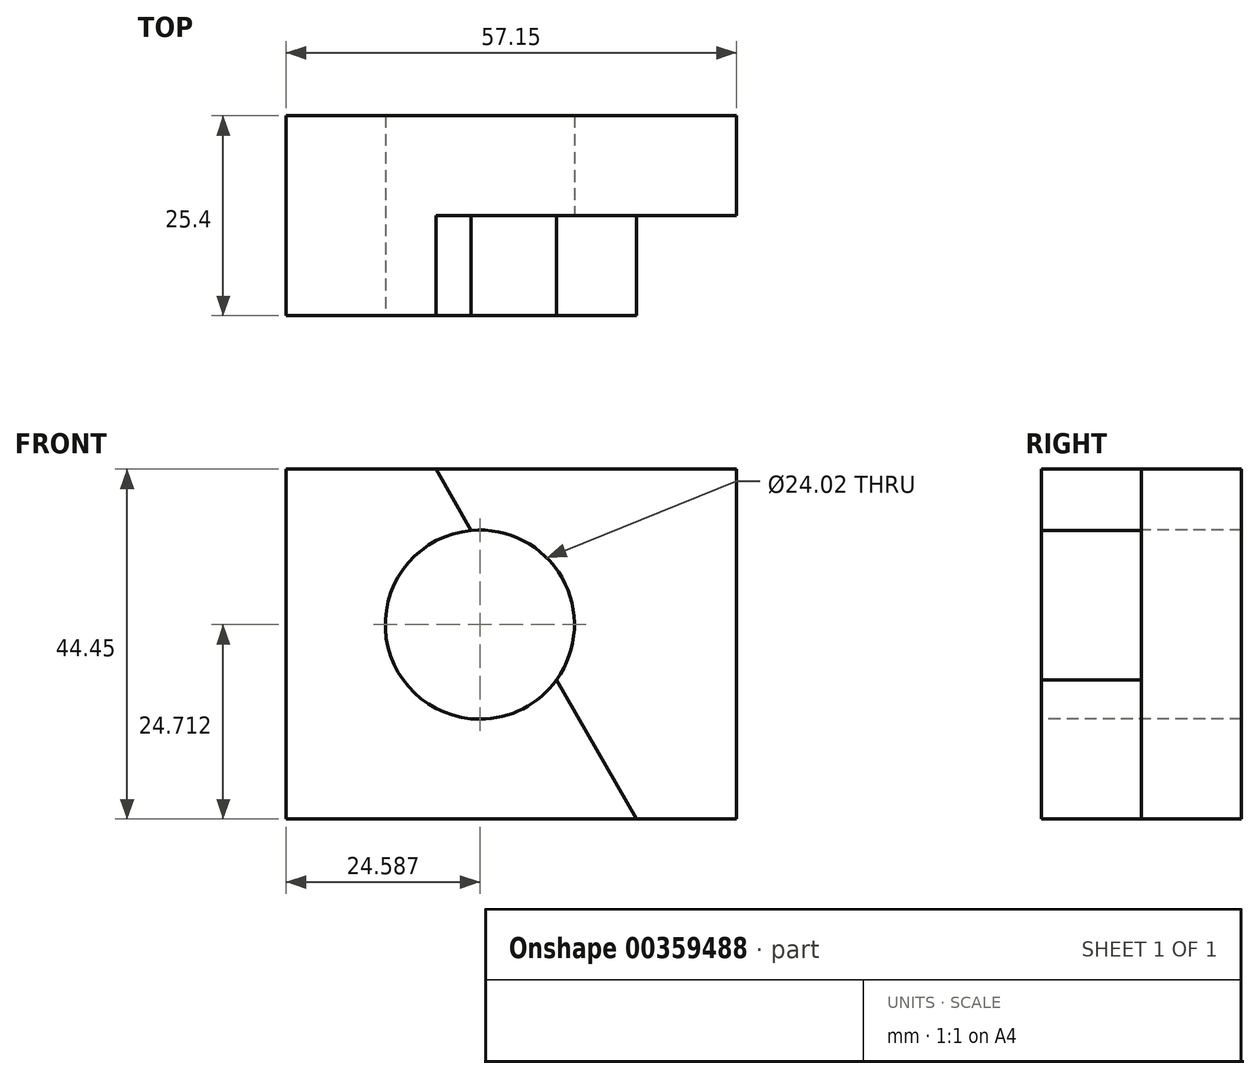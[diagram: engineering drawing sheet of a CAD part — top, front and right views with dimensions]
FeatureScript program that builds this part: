
annotation { "Feature Type Name" : "Feature", "Feature Type Description" : "" }
export const myFeature = defineFeature(function(context is Context, id is Id, definition is map)
    precondition{}
    {
        {
            var Q0;
            Q0=qCreatedBy(makeId("Front.planeOp"),FACE);
            var sketch = newSketch(context, id + "F0", { "sketchPlane" : qUnion([Q0])});
            skLineSegment(sketch, "E0", {"start": v(0, 44.45) * mm, "end": v(0, 0) * mm});
            skLineSegment(sketch, "E1", {"start": v(0, 0) * mm, "end": v(57.15, 0) * mm});
            skLineSegment(sketch, "E2", {"start": v(57.15, 0) * mm, "end": v(57.15, 44.45) * mm});
            skLineSegment(sketch, "E3", {"start": v(57.15, 44.45) * mm, "end": v(0, 44.45) * mm});
            skSolve(sketch);
        }
        {
            var Q0;
            Q0 = qSketchRegion(id + "F0", true);
            extrude(context, id + "F1", {"entities" : qUnion([Q0]), "oppositeDirection" : true, "depth" : 25.4 * mm});
        }
        {
            var Q0;
            Q0=qCreatedBy(makeId("Front.planeOp"),FACE);
            var sketch = newSketch(context, id + "F2", { "sketchPlane" : qUnion([Q0])});
            skLineSegment(sketch, "E4", {"start": v(44.45, 44.45) * mm, "end": v(44.45, 0) * mm});
            skLineSegment(sketch, "E5", {"start": v(44.45, 0) * mm, "end": v(57.15, 0) * mm});
            skLineSegment(sketch, "E6", {"start": v(57.15, 0) * mm, "end": v(57.15, 44.45) * mm});
            skLineSegment(sketch, "E7", {"start": v(57.15, 44.45) * mm, "end": v(44.45, 44.45) * mm});
            skSolve(sketch);
        }
        {
            var Q0;
            Q0 = qSketchRegion(id + "F2", true);
            extrude(context, id + "F3", {"entities" : qUnion([Q0]), "operationType" : NewBodyOperationType.REMOVE, "oppositeDirection" : true, "depth" : 12.7 * mm});
        }
        {
            var Q0;
            Q0=qCreatedBy(makeId("Front.planeOp"),FACE);
            var sketch = newSketch(context, id + "F4", { "sketchPlane" : qUnion([Q0])});
            skLineSegment(sketch, "E8", {"start": v(44.45, 0) * mm, "end": v(44.45, 44.45) * mm});
            skLineSegment(sketch, "E9", {"start": v(44.45, 44.45) * mm, "end": v(19.05, 44.45) * mm});
            skLineSegment(sketch, "E10", {"start": v(19.05, 44.45) * mm, "end": v(44.45, 0) * mm});
            skSolve(sketch);
        }
        {
            var Q0;
            Q0 = qSketchRegion(id + "F4", true);
            extrude(context, id + "F5", {"entities" : qUnion([Q0]), "operationType" : NewBodyOperationType.REMOVE, "oppositeDirection" : true, "depth" : 12.7 * mm});
        }
        {
            var Q0;
            Q0=qCreatedBy(makeId("Front.planeOp"),FACE);
            var sketch = newSketch(context, id + "F6", { "sketchPlane" : qUnion([Q0])});
            skCircle(sketch, "E11", {"center": v(24.59, 24.71) * mm, "radius": 12.01 * mm});
            skSolve(sketch);
        }
        {
            var Q0;
            Q0 = qSketchRegion(id + "F6", true);
            extrude(context, id + "F7", {"entities" : qUnion([Q0]), "operationType" : NewBodyOperationType.REMOVE, "oppositeDirection" : true, "depth" : 25.4 * mm});
        }
    });
